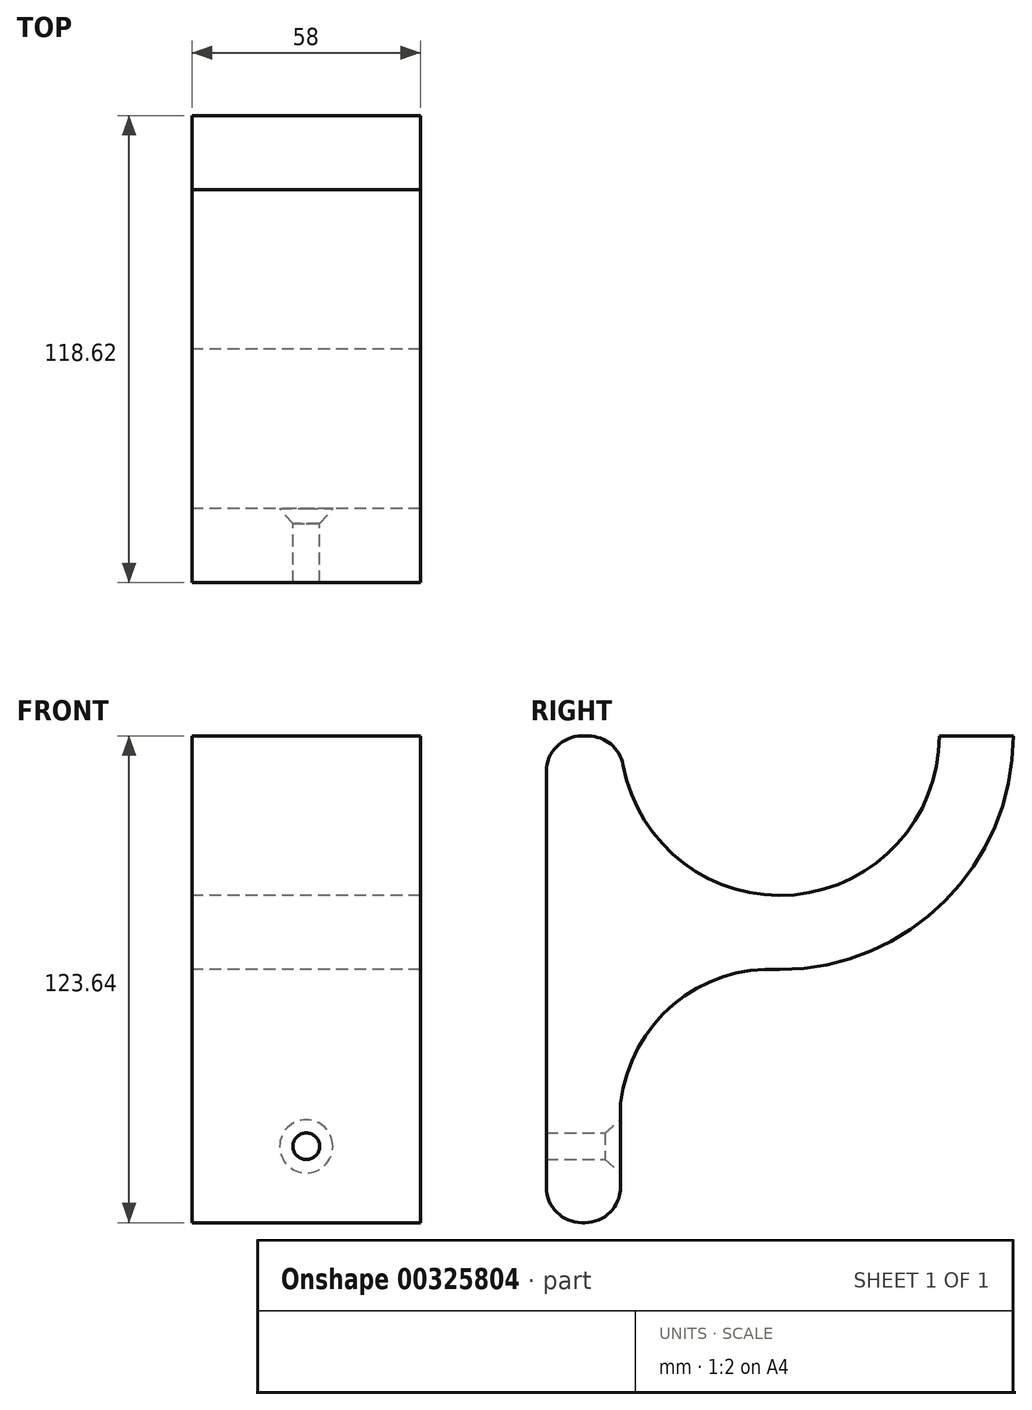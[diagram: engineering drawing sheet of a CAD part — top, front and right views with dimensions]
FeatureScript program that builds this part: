
annotation { "Feature Type Name" : "Feature", "Feature Type Description" : "" }
export const myFeature = defineFeature(function(context is Context, id is Id, definition is map)
    precondition{}
    {
        {
            var Q0;
            Q0=qCreatedBy(makeId("Right.planeOp"),FACE);
            var sketch = newSketch(context, id + "F0", { "sketchPlane" : qUnion([Q0])});
            skCircle(sketch, "E0", {"center": v(0, 0) * mm, "radius": 40.5 * mm});
            skPoint(sketch, "E1", {"position": v(40.5, 0) * mm});
            skPoint(sketch, "E2", {"position": v(-40.5, 0) * mm});
            skLineSegment(sketch, "E3", {"start": v(0, 0) * mm, "end": v(0, -46.45) * mm});
            skCircle(sketch, "E4", {"center": v(0, 0) * mm, "radius": 59.31 * mm});
            skLineSegment(sketch, "E5", {"start": v(0, 0) * mm, "end": v(59.31, 0) * mm});
            skLineSegment(sketch, "E6", {"start": v(59.31, 0) * mm, "end": v(-59.31, 0) * mm});
            skLineSegment(sketch, "E7", {"start": v(-59.31, 0) * mm, "end": v(-59.31, 38.1) * mm});
            skLineSegment(sketch, "E8", {"start": v(-40.5, 0) * mm, "end": v(-40.5, 38.1) * mm});
            skLineSegment(sketch, "E9", {"start": v(-40.5, 38.1) * mm, "end": v(-59.31, 38.1) * mm});
            skLineSegment(sketch, "E10", {"start": v(-59.31, 0) * mm, "end": v(-59.31, -123.64) * mm});
            skLineSegment(sketch, "E11.bottom", {"start": v(-59.31, -123.64) * mm, "end": v(-40.5, -123.64) * mm});
            skLineSegment(sketch, "E11.top", {"start": v(-59.31, 38.1) * mm, "end": v(-40.5, 38.1) * mm});
            skLineSegment(sketch, "E11.left", {"start": v(-59.31, -123.64) * mm, "end": v(-59.31, 38.1) * mm});
            skLineSegment(sketch, "E11.right", {"start": v(-40.5, -123.64) * mm, "end": v(-40.5, 38.1) * mm});
            skArc(sketch, "E12", {"start": v(0, -59.31) * mm, "mid": v(-27.23, -68.4) * mm, "end": v(-40.5, -93.84) * mm});
            skSolve(sketch);
        }
        {
            var Q0;
            {var subQ0=sQuery(id+"F0.wireOp",EDGE,"6KHeeEcf-SE6f-c5qw-g0Xh-YKAvhVHegDeh.bottom");Q0=makeQuery(id+"F0.imprint","IMPRINT",FACE,{"disambiguationData":[TD([[makeQuery(id+"F0.imprint","IMPRINT",EDGE,{"derivedFrom":subQ0}),1.0]])]});}
            var Q1;
            {var subQ3=sQuery(id+"F0.wireOp",EDGE,"UKnFotwT-FIUX-u8OZ-C6A4-vtIvSYW7LpxD");Q1=makeQuery(id+"F0.imprint","IMPRINT",FACE,{"disambiguationData":[TD([[makeQuery(id+"F0.imprint","IMPRINT",EDGE,{"derivedFrom":subQ3}),-1.0]])]});}
            var Q2;
            {var subQ3=sQuery(id+"F0.wireOp",EDGE,"CNRmDwGO-a11G-3Uha-2VvQ-FMbn2noqrJcd.bottom");Q2=makeQuery(id+"F0.imprint","IMPRINT",FACE,{"disambiguationData":[TD([[makeQuery(id+"F0.imprint","IMPRINT",EDGE,{"derivedFrom":subQ3}),1.0]])]});}
            var Q3;
            {var subQ5=sQuery(id+"F0.wireOp",EDGE,"6KHeeEcf-SE6f-c5qw-g0Xh-YKAvhVHegDeh.top");Q3=makeQuery(id+"F0.imprint","IMPRINT",FACE,{"disambiguationData":[TD([[makeQuery(id+"F0.imprint","IMPRINT",EDGE,{"derivedFrom":subQ5}),1.0]])]});}
            var Q4;
            {var subQ0=sQuery(id+"F0.wireOp",EDGE,"6KHeeEcf-SE6f-c5qw-g0Xh-YKAvhVHegDeh.bottom");Q4=makeQuery(id+"F0.imprint","IMPRINT",FACE,{"disambiguationData":[TD([[makeQuery(id+"F0.imprint","IMPRINT",EDGE,{"derivedFrom":subQ0}),-1.0]])]});}
            var Q5;
            {var subQ4=sQuery(id+"F0.wireOp",EDGE,"rM1FiaFO-1ARb-bEe9-xJRG-An0HylYMHqUA.top");Q5=makeQuery(id+"F0.imprint","IMPRINT",FACE,{"disambiguationData":[TD([[makeQuery(id+"F0.imprint","IMPRINT",EDGE,{"derivedFrom":subQ4}),-1.0]])]});}
            var Q6;
            {var subQ0=sQuery(id+"F0.wireOp",EDGE,"rM1FiaFO-1ARb-bEe9-xJRG-An0HylYMHqUA.bottom");Q6=makeQuery(id+"F0.imprint","IMPRINT",FACE,{"disambiguationData":[TD([[makeQuery(id+"F0.imprint","IMPRINT",EDGE,{"derivedFrom":subQ0}),1.0]])]});}
            var Q7;
            {var subQ0=sQuery(id+"F0.wireOp",EDGE,"rM1FiaFO-1ARb-bEe9-xJRG-An0HylYMHqUA.left");var subQ1=sQuery(id+"F0.wireOp",EDGE,"E0");var subQ2=makeQuery(id+"F0.imprint","INTERSECT",VERTEX,{"derivedFrom":[subQ1,subQ0]});Q7=makeQuery(id+"F0.imprint","IMPRINT",FACE,{"disambiguationData":[TD([[makeQuery(id+"F0.imprint","IMPRINT",EDGE,{"disambiguationData":[TD([[subQ2,1.0]])],"derivedFrom":subQ1}),-1.0]])]});}
            var Q8;
            Q8=makeQuery(id+"F0.imprint","IMPRINT",FACE,{"disambiguationData":[TD([[makeQuery(id+"F0.imprint","IMPRINT",EDGE,{"derivedFrom":sQuery(id+"F0.wireOp",EDGE,"q0gY8Whx-I7MX-2CSH-bm76-PX7j0ED2jb0m.bottom")}),1.0]])]});
            var Q9;
            {var subQ0=sQuery(id+"F0.wireOp",EDGE,"hm3VU3S3-TMUl-XZE1-T3Kb-TfNGBGDjZRVu");Q9=makeQuery(id+"F0.imprint","IMPRINT",FACE,{"disambiguationData":[TD([[makeQuery(id+"F0.imprint","IMPRINT",EDGE,{"derivedFrom":subQ0}),1.0]])]});}
            var Q10;
            {var subQ1=sQuery(id+"F0.wireOp",EDGE,"E4");var subQ3=sQuery(id+"F0.wireOp",EDGE,"E11.right");var subQ4=makeQuery(id+"F0.imprint","INTERSECT",VERTEX,{"disambiguationData":[OD(1.0)],"derivedFrom":[subQ1,subQ3]});Q10=makeQuery(id+"F0.imprint","IMPRINT",FACE,{"disambiguationData":[TD([[makeQuery(id+"F0.imprint","IMPRINT",EDGE,{"disambiguationData":[TD([[subQ4,1.0]])],"derivedFrom":subQ1}),1.0]])]});}
            var Q11;
            {var subQ5=sQuery(id+"F0.wireOp",EDGE,"E11.top");Q11=makeQuery(id+"F0.imprint","IMPRINT",FACE,{"disambiguationData":[TD([[makeQuery(id+"F0.imprint","IMPRINT",EDGE,{"derivedFrom":subQ5}),-1.0]])]});}
            var Q12;
            {var subQ1=sQuery(id+"F0.wireOp",EDGE,"E4");var subQ3=sQuery(id+"F0.wireOp",EDGE,"E11.right");var subQ4=makeQuery(id+"F0.imprint","INTERSECT",VERTEX,{"disambiguationData":[OD(0.0)],"derivedFrom":[subQ1,subQ3]});Q12=makeQuery(id+"F0.imprint","IMPRINT",FACE,{"disambiguationData":[TD([[makeQuery(id+"F0.imprint","IMPRINT",EDGE,{"disambiguationData":[TD([[subQ4,-1.0]])],"derivedFrom":subQ1}),1.0]])]});}
            var Q13;
            {var subQ5=sQuery(id+"F0.wireOp",EDGE,"E11.bottom");Q13=makeQuery(id+"F0.imprint","IMPRINT",FACE,{"disambiguationData":[TD([[makeQuery(id+"F0.imprint","IMPRINT",EDGE,{"derivedFrom":subQ5}),1.0]])]});}
            var Q14;
            {var subQ0=sQuery(id+"F0.wireOp",EDGE,"v5CoBPKe-ZFwp-j0W8-JkQ9-2mehnFdtI1sS");Q14=makeQuery(id+"F0.imprint","IMPRINT",FACE,{"disambiguationData":[TD([[makeQuery(id+"F0.imprint","IMPRINT",EDGE,{"derivedFrom":subQ0}),-1.0]])]});}
            var Q15;
            {var subQ0=sQuery(id+"F0.wireOp",EDGE,"E12");Q15=makeQuery(id+"F0.imprint","IMPRINT",FACE,{"disambiguationData":[TD([[makeQuery(id+"F0.imprint","IMPRINT",EDGE,{"derivedFrom":subQ0}),-1.0]])]});}
            var Q16;
            {var subQ3=sQuery(id+"F0.wireOp",EDGE,"E11.top");var subQ5=sQuery(id+"F0.wireOp",EDGE,"E11.right");var subQ6=makeQuery(id+"F0.imprint","INTERSECT",VERTEX,{"derivedFrom":[subQ3,subQ5]});Q16=makeQuery(id+"F0.imprint","IMPRINT",FACE,{"disambiguationData":[TD([[makeQuery(id+"F0.imprint","IMPRINT",EDGE,{"disambiguationData":[TD([[subQ6,1.0]])],"derivedFrom":subQ3}),-1.0]])]});}
            extrude(context, id + "F1", {"entities" : qUnion([Q0, Q1, Q2, Q3, Q4, Q5, Q6, Q7, Q8, Q9, Q10, Q11, Q12, Q13, Q14, Q15, Q16]), "depth" : 58 * mm});
        }
        {
            var Q0;
            Q0=makeQuery(id+"F1.opExtrude","SWEPT_EDGE",EDGE,{"disambiguationData":[OSD([sQuery(id+"F0.wireOp",EDGE,"E11.top"),sQuery(id+"F0.wireOp",EDGE,"E11.right")])]});
            var Q1;
            Q1=makeQuery(id+"F1.opExtrude","SWEPT_EDGE",EDGE,{"disambiguationData":[OSD([sQuery(id+"F0.wireOp",EDGE,"E11.top"),sQuery(id+"F0.wireOp",EDGE,"E11.left")])]});
            var Q2;
            Q2=makeQuery(id+"F1.opExtrude","SWEPT_EDGE",EDGE,{"disambiguationData":[OSD([sQuery(id+"F0.wireOp",EDGE,"E4"),sQuery(id+"F0.wireOp",EDGE,"E6")])]});
            var Q3;
            Q3=makeQuery(id+"F1.opExtrude","SWEPT_EDGE",EDGE,{"disambiguationData":[OSD([sQuery(id+"F0.wireOp",EDGE,"E0"),sQuery(id+"F0.wireOp",EDGE,"E6")])]});
            var Q4;
            Q4=makeQuery(id+"F1.opExtrude","SWEPT_EDGE",EDGE,{"disambiguationData":[OSD([sQuery(id+"F0.wireOp",EDGE,"E11.bottom"),sQuery(id+"F0.wireOp",EDGE,"E11.right"),sQuery(id+"F0.wireOp",EDGE,"v5CoBPKe-ZFwp-j0W8-JkQ9-2mehnFdtI1sS")])]});
            var Q5;
            Q5=makeQuery(id+"F1.opExtrude","SWEPT_EDGE",EDGE,{"disambiguationData":[OSD([sQuery(id+"F0.wireOp",EDGE,"E11.bottom"),sQuery(id+"F0.wireOp",EDGE,"E11.left")])]});
            fillet(context, id + "F2", {"entities" : qUnion([Q0, Q1, Q2, Q3, Q4, Q5]), "radius" : 9 * mm, "tangentPropagation" : true, "allowEdgeOverflow" : false});
        }
        {
            var Q0;
            {var subQ0=sQuery(id+"F0.wireOp",EDGE,"E11.right");Q0=makeQuery(id+"F1.opExtrude","SWEPT_FACE",FACE,{"disambiguationData":[OSD([subQ0]),TDD([makeQuery(id+"F0.imprint","IMPRINT",EDGE,{"disambiguationData":[TD([[makeQuery(id+"F0.imprint","INTERSECT",VERTEX,{"derivedFrom":[sQuery(id+"F0.wireOp",EDGE,"E11.bottom"),subQ0]}),-1.0]])],"derivedFrom":subQ0})])]});}
            var sketch = newSketch(context, id + "F3", { "sketchPlane" : qUnion([Q0])});
            skLineSegment(sketch, "E13", {"start": v(-29, -114.64) * mm, "end": v(-29, 32.07) * mm});
            skLineSegment(sketch, "E14", {"start": v(-29, 32.07) * mm, "end": v(-29, 0) * mm});
            skLineSegment(sketch, "E15", {"start": v(-29, -114.64) * mm, "end": v(-29, -93.84) * mm});
            skPoint(sketch, "E16", {"position": v(-29, 16.04) * mm});
            skPoint(sketch, "E17", {"position": v(-29, -104.24) * mm});
            skSolve(sketch);
        }
        {
            var Q0;
            Q0=sQuery(id+"F3.wireOp",VERTEX,"E16");
            var Q1;
            Q1=sQuery(id+"F3.wireOp",VERTEX,"E17");
            var Q2;
            Q2=makeQuery(id+"F1.opExtrude","SWEPT_BODY",BODY,{"disambiguationData":[OSD([sQuery(id+"F0.wireOp",EDGE,"E0"),sQuery(id+"F0.wireOp",EDGE,"E4"),sQuery(id+"F0.wireOp",EDGE,"E6"),sQuery(id+"F0.wireOp",EDGE,"E11.bottom"),sQuery(id+"F0.wireOp",EDGE,"E11.top"),sQuery(id+"F0.wireOp",EDGE,"E11.left"),sQuery(id+"F0.wireOp",EDGE,"E11.right"),sQuery(id+"F0.wireOp",EDGE,"E12")])]});
            hole(context, id + "F4", {"style" : HoleStyle.C_SINK, "endStyle" : HoleEndStyle.BLIND, "standardTappedOrClearance" : lookupTablePath({ "standard" : "ANSI", "fit" : "Normal (ASME)", "size" : "1/4", "type" : "Clearance" }), "standardBlindInLast" : lookupTablePath({ "fit" : "Free", "standard" : "ANSI", "size" : "1/4", "type" : "Clearance" }), "holeDiameter" : 6.76 * mm, "cSinkDiameter" : 13.5 * mm, "cSinkAngle" : 82 * degree, "holeDepth" : 127 * mm, "tappedDepth" : 12.7 * mm, "tapClearance" : 3, "locations" : qUnion([Q0, Q1]), "scope" : qUnion([Q2])});
        }
    });
